# Revit family: Lighting_Wall-Mounted_Nordlux_Stay-Long_Wall
name_source: partatom
category: Lighting Fixtures
revit_build: Autodesk Revit 2017 (Build: 20160225_1515(x64)
units: mm (PartAtom-declared; Revit-internal decimal feet)

## family parameters
Cut with Voids When Loaded = No
Host = Face
Light Source = Yes
OmniClass Number = 23.80.70.00
OmniClass Title = Lighting
Part Type = Normal
Room Calculation Point = No
Round Connector Dimension = Use Diameter
Shared = No

## types (2) — shared parameters
AssetType = Fixed
BIMObjectName = Lighting_Wall-Mounted_Nordlux_Stay-Long_Wall
Brand = Nordlux
Category = Wall lighting
Collection = Stay Long
Color Filter = 16777215
ConvergoRefNr = 0143-2009-0013-DK
Designer = Maria Berntsen
Dimming Lamp Color Temperature Shift = <None>
DurationUnit = Hours
ElectricalDeviceNominalPower = 40
Features = Cable length: 250 cm. Socket type E27. Light source not included. Energy class A++ - A.
HasProtectiveEarth = Yes
IP_Code = IP20
IfcExportAs = IfcLightFixtureType
IfcExportType = NOTDEFINED
InsulationStandardClass = Class 2 (Double insulated)
LensMaterial = Glass
LightFixtureMountingType = Fixed
LightFixturePlacingType = Wall
Manufacturer = Nordlux
ManufacturerName = Nordlux
ManufacturerURL = https://www.nordlux.dk
Material = Metal
NBSDescription = General purpose luminaires
NBSReference = 90-60-50/405
Name = Stay-Long_Wall
NominalCurrent = 1 A
NominalFrequencyRange = 50 Hz
NominalHeight = 616 mm
NominalLength = 705 mm
NominalVoltage = 230 V
NominalVoltageCalc = 230 V
NominalWidth = 250 mm
NumberOfPoles = 1
PhaseAngle = 0.00°
Photometric Web File = 2020455003 and 010 Stay Long Wall.ies
ProductDatasheet = http://pim.skypim.com
Shape = Sculptured
Size = 705x250x615 mm
Tilt Angle = 90.00°
TotalWattage = 40 W
URL = https://www.nordlux.com
Uniclass2 = Pr_70_70_49_43
Uniclass2015Description = Light-Emitting Diode (LED) Luminaires
Uniclass2015Reference = Pr_70_70_48_46
UsageCurrent = 0 A
Version = 1
VersionDate = 24/11/2020
WarrantyDurationUnit = Hours
zero-valued in all types: Cost, Default Elevation, MaintenanceFactor, NominalDiameter, NominalRadius, NumberOfSources

## per-type parameters (varying)
| type | ArticleNumber | Color | Description | EANNumber | Finish | LightFixtureMainMaterial | ModelReference | ProductInformation |
| Stay Long Wall - Black | 2020455003 | Black | Stay in black silky matte metal is an exciting alternative to the classic wall lamp, which with its functional design results in beautiful lighting. Stay has a high functional value, as the arm and head of the lamp can be adjusted as needed, making the wall lamp perfect as task lighting in the kitchen or next to the bed. | 5704924000980 | Cable colour: Black textile cable | Black | 2020455003 | Stay in black silky matte metal is an exciting alternative to the classic wall lamp, which with its functional design results in beautiful lighting. Stay has a high functional value, as the arm and head of the lamp can be adjusted as needed, making the wall lamp perfect as task lighting in the kitchen or next to the bed. |
| Stay Long Wall - Grey | 2020455010 | Grey | Stay in grey silky matte metal is an exciting alternative to the classic wall lamp, which with its functional design results in beautiful lighting. Stay has a high functional value, as the arm and head of the lamp can be adjusted as needed, making the wall lamp perfect as task lighting in the kitchen or next to the bed. | 5704924000997 | Cable colour: Grey textile cable | Grey | 2020455010 | Stay in grey silky matte metal is an exciting alternative to the classic wall lamp, which with its functional design results in beautiful lighting. Stay has a high functional value, as the arm and head of the lamp can be adjusted as needed, making the wall lamp perfect as task lighting in the kitchen or next to the bed. |

note: column(s) folded — value = type name in every type: Model

## geometry (parser evidence)
native form markers: Sweep x4
no freeform markers — native parametric forms only
